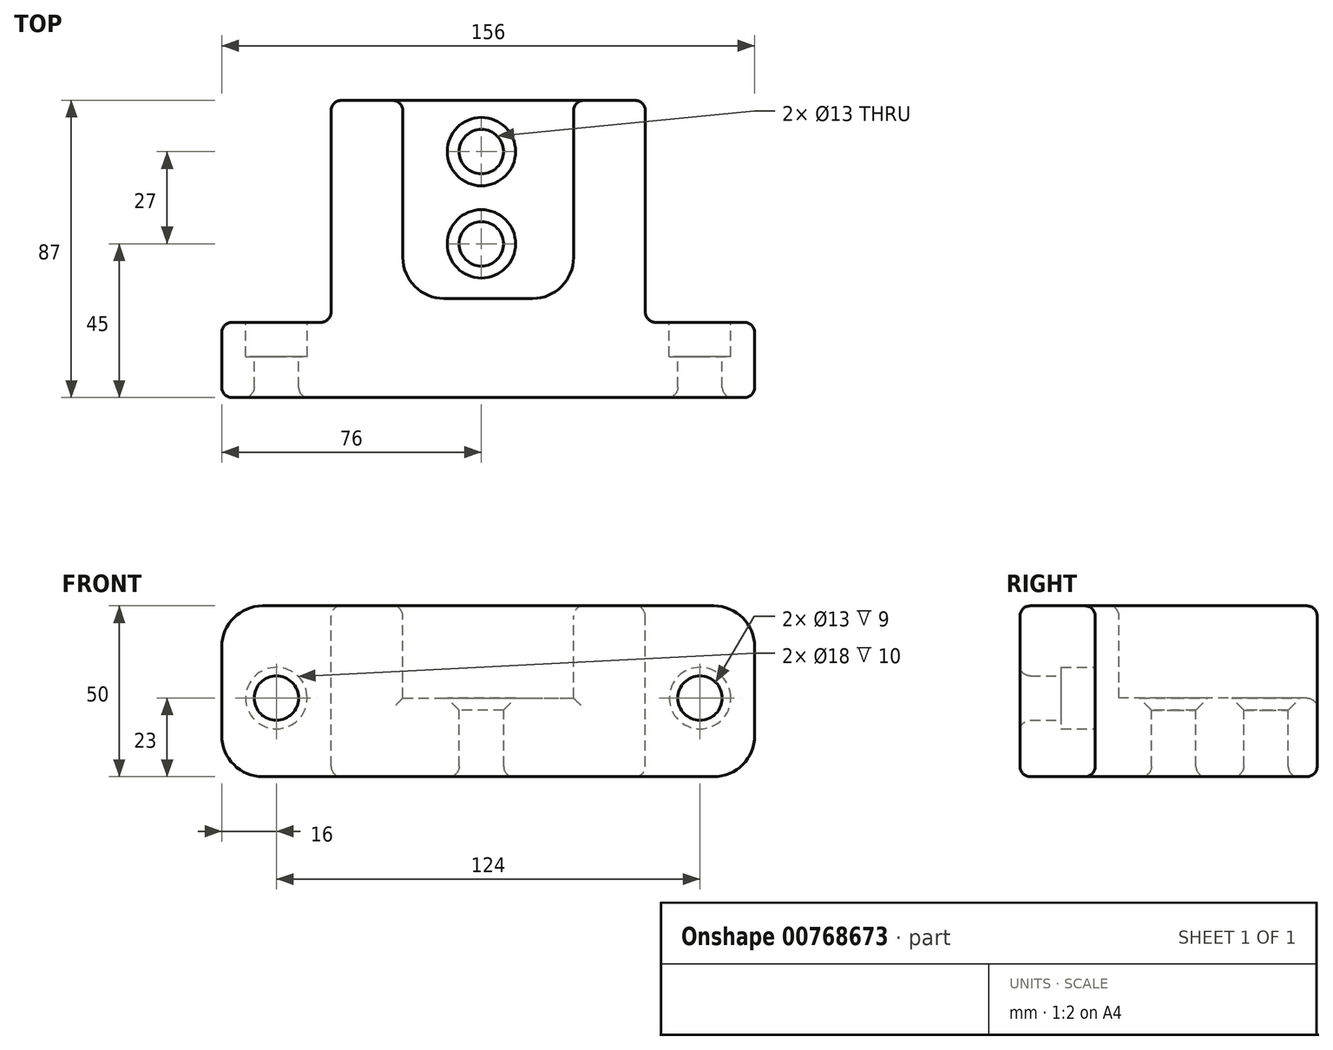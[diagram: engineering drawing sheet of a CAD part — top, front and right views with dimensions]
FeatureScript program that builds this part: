
annotation { "Feature Type Name" : "Feature", "Feature Type Description" : "" }
export const myFeature = defineFeature(function(context is Context, id is Id, definition is map)
    precondition{}
    {
        {
            var Q0;
            Q0=qCreatedBy(makeId("Front.planeOp"),FACE);
            var sketch = newSketch(context, id + "F0", { "sketchPlane" : qUnion([Q0])});
            skLineSegment(sketch, "E0.bottom", {"start": v(0, 0) * mm, "end": v(156, 0) * mm});
            skLineSegment(sketch, "E0.top", {"start": v(0, 50) * mm, "end": v(156, 50) * mm});
            skLineSegment(sketch, "E0.left", {"start": v(0, 0) * mm, "end": v(0, 50) * mm});
            skLineSegment(sketch, "E0.right", {"start": v(156, 0) * mm, "end": v(156, 50) * mm});
            skSolve(sketch);
        }
        {
            var Q0;
            Q0 = qSketchRegion(id + "F0", true);
            extrude(context, id + "F1", {"entities" : qUnion([Q0]), "depth" : 87 * mm, "offsetDistance" : 25 * mm});
        }
        {
            var Q0;
            Q0=makeQuery(id+"F1.opExtrude","SWEPT_FACE",FACE,{"disambiguationData":[OSD([sQuery(id+"F0.wireOp",EDGE,"E0.top")])]});
            var sketch = newSketch(context, id + "F2", { "sketchPlane" : qUnion([Q0])});
            skLineSegment(sketch, "E1.bottom", {"start": v(156, 0) * mm, "end": v(124, 0) * mm});
            skLineSegment(sketch, "E1.top", {"start": v(156, -65) * mm, "end": v(124, -65) * mm});
            skLineSegment(sketch, "E1.left", {"start": v(156, 0) * mm, "end": v(156, -65) * mm});
            skLineSegment(sketch, "E1.right", {"start": v(124, 0) * mm, "end": v(124, -65) * mm});
            skLineSegment(sketch, "E2.bottom", {"start": v(0, 0) * mm, "end": v(32, 0) * mm});
            skLineSegment(sketch, "E2.top", {"start": v(0, -65) * mm, "end": v(32, -65) * mm});
            skLineSegment(sketch, "E2.left", {"start": v(0, 0) * mm, "end": v(0, -65) * mm});
            skLineSegment(sketch, "E2.right", {"start": v(32, 0) * mm, "end": v(32, -65) * mm});
            skSolve(sketch);
        }
        {
            var Q0;
            Q0 = qSketchRegion(id + "F2", true);
            extrude(context, id + "F3", {"entities" : qUnion([Q0]), "operationType" : NewBodyOperationType.REMOVE, "endBound" : BoundingType.UP_TO_NEXT, "oppositeDirection" : true, "depth" : 25 * mm, "offsetDistance" : 25 * mm});
        }
        {
            var Q0;
            Q0=makeQuery(id+"F1.opExtrude","SWEPT_FACE",FACE,{"disambiguationData":[OSD([sQuery(id+"F0.wireOp",EDGE,"E0.top")])]});
            var sketch = newSketch(context, id + "F4", { "sketchPlane" : qUnion([Q0])});
            skLineSegment(sketch, "E3.bottom", {"start": v(53, 0) * mm, "end": v(103, 0) * mm});
            skLineSegment(sketch, "E3.top", {"start": v(53, -58) * mm, "end": v(103, -58) * mm});
            skLineSegment(sketch, "E3.left", {"start": v(53, 0) * mm, "end": v(53, -58) * mm});
            skLineSegment(sketch, "E3.right", {"start": v(103, 0) * mm, "end": v(103, -58) * mm});
            skSolve(sketch);
        }
        {
            var Q0;
            Q0 = qSketchRegion(id + "F4", true);
            extrude(context, id + "F5", {"entities" : qUnion([Q0]), "operationType" : NewBodyOperationType.REMOVE, "oppositeDirection" : true, "depth" : 27 * mm, "offsetDistance" : 25 * mm});
        }
        {
            var Q0;
            Q0=makeQuery(id+"F3.boolean.opBoolean","COPY",FACE,{"derivedFrom":makeQuery(id+"F3.opExtrude","SWEPT_FACE",FACE,{"disambiguationData":[OSD([sQuery(id+"F2.wireOp",EDGE,"E1.top")])]})});
            var sketch = newSketch(context, id + "F6", { "sketchPlane" : qUnion([Q0])});
            skPoint(sketch, "E4", {"position": v(-140, 23) * mm});
            skPoint(sketch, "E5", {"position": v(-16, 23) * mm});
            skSolve(sketch);
        }
        {
            var Q0;
            Q0=sQuery(id+"F6.wireOp",VERTEX,"E4");
            var Q1;
            Q1=sQuery(id+"F6.wireOp",VERTEX,"E5");
            var Q2;
            Q2=makeQuery(id+"F1.opExtrude","SWEPT_BODY",BODY,{"disambiguationData":[OSD([sQuery(id+"F0.wireOp",EDGE,"E0.bottom"),sQuery(id+"F0.wireOp",EDGE,"E0.top"),sQuery(id+"F0.wireOp",EDGE,"E0.left"),sQuery(id+"F0.wireOp",EDGE,"E0.right")])]});
            hole(context, id + "F7", {"style" : HoleStyle.C_BORE, "endStyle" : HoleEndStyle.THROUGH, "holeDiameter" : 13 * mm, "cBoreDiameter" : 18 * mm, "cBoreDepth" : 10 * mm, "majorDiameter" : 5 * mm, "isTappedThrough" : true, "tappedDepth" : 12 * mm, "tapClearance" : 3, "locations" : qUnion([Q0, Q1]), "scope" : qUnion([Q2])});
        }
        {
            var Q0;
            Q0=makeQuery(id+"F5.boolean.opBoolean","COPY",FACE,{"derivedFrom":makeQuery(id+"F5.opExtrude","CAP_FACE",FACE,{"disambiguationData":[OSD([sQuery(id+"F4.wireOp",EDGE,"E3.bottom"),sQuery(id+"F4.wireOp",EDGE,"E3.top"),sQuery(id+"F4.wireOp",EDGE,"E3.left"),sQuery(id+"F4.wireOp",EDGE,"E3.right")])],"isStart":false})});
            var sketch = newSketch(context, id + "F8", { "sketchPlane" : qUnion([Q0])});
            skPoint(sketch, "E6", {"position": v(76, -15) * mm});
            skPoint(sketch, "E7", {"position": v(76, -42) * mm});
            skSolve(sketch);
        }
        {
            var Q0;
            Q0=sQuery(id+"F8.wireOp",VERTEX,"E6");
            var Q1;
            Q1=sQuery(id+"F8.wireOp",VERTEX,"E7");
            var Q2;
            Q2=makeQuery(id+"F1.opExtrude","SWEPT_BODY",BODY,{"disambiguationData":[OSD([sQuery(id+"F0.wireOp",EDGE,"E0.bottom"),sQuery(id+"F0.wireOp",EDGE,"E0.top"),sQuery(id+"F0.wireOp",EDGE,"E0.left"),sQuery(id+"F0.wireOp",EDGE,"E0.right")])]});
            hole(context, id + "F9", {"style" : HoleStyle.C_SINK, "endStyle" : HoleEndStyle.THROUGH, "holeDiameter" : 13 * mm, "cSinkDiameter" : 20 * mm, "cSinkAngle" : 90 * degree, "majorDiameter" : 5 * mm, "isTappedThrough" : true, "tappedDepth" : 12 * mm, "tapClearance" : 3, "locations" : qUnion([Q0, Q1]), "scope" : qUnion([Q2])});
        }
        {
            var Q0;
            Q0=makeQuery(id+"F1.opExtrude","SWEPT_EDGE",EDGE,{"disambiguationData":[OSD([sQuery(id+"F0.wireOp",EDGE,"E0.top"),sQuery(id+"F0.wireOp",EDGE,"E0.right")])]});
            var Q1;
            Q1=makeQuery(id+"F1.opExtrude","SWEPT_EDGE",EDGE,{"disambiguationData":[OSD([sQuery(id+"F0.wireOp",EDGE,"E0.bottom"),sQuery(id+"F0.wireOp",EDGE,"E0.right")])]});
            var Q2;
            Q2=makeQuery(id+"F1.opExtrude","SWEPT_EDGE",EDGE,{"disambiguationData":[OSD([sQuery(id+"F0.wireOp",EDGE,"E0.top"),sQuery(id+"F0.wireOp",EDGE,"E0.left")])]});
            var Q3;
            Q3=makeQuery(id+"F1.opExtrude","SWEPT_EDGE",EDGE,{"disambiguationData":[OSD([sQuery(id+"F0.wireOp",EDGE,"E0.bottom"),sQuery(id+"F0.wireOp",EDGE,"E0.left")])]});
            var Q4;
            Q4=makeQuery(id+"F5.boolean.opBoolean","COPY",EDGE,{"derivedFrom":makeQuery(id+"F5.opExtrude","SWEPT_EDGE",EDGE,{"disambiguationData":[OSD([sQuery(id+"F4.wireOp",EDGE,"E3.top"),sQuery(id+"F4.wireOp",EDGE,"E3.left")])]})});
            var Q5;
            Q5=makeQuery(id+"F5.boolean.opBoolean","COPY",EDGE,{"derivedFrom":makeQuery(id+"F5.opExtrude","SWEPT_EDGE",EDGE,{"disambiguationData":[OSD([sQuery(id+"F4.wireOp",EDGE,"E3.top"),sQuery(id+"F4.wireOp",EDGE,"E3.right")])]})});
            fillet(context, id + "F10", {"entities" : qUnion([Q0, Q1, Q2, Q3, Q4, Q5]), "radius" : 12 * mm, "tangentPropagation" : true, "allowEdgeOverflow" : false});
        }
        {
            var Q0;
            Q0=makeQuery(id+"F1.opExtrude","CAP_FACE",FACE,{"disambiguationData":[OSD([sQuery(id+"F0.wireOp",EDGE,"E0.bottom"),sQuery(id+"F0.wireOp",EDGE,"E0.top"),sQuery(id+"F0.wireOp",EDGE,"E0.left"),sQuery(id+"F0.wireOp",EDGE,"E0.right")])],"isStart":true});
            var Q1;
            Q1=makeQuery(id+"F1.opExtrude","SWEPT_FACE",FACE,{"disambiguationData":[OSD([sQuery(id+"F0.wireOp",EDGE,"E0.top")])]});
            var Q2;
            Q2=makeQuery(id+"F3.boolean.opBoolean","COPY",FACE,{"derivedFrom":makeQuery(id+"F3.opExtrude","SWEPT_FACE",FACE,{"disambiguationData":[OSD([sQuery(id+"F2.wireOp",EDGE,"E2.right")])]})});
            var Q3;
            Q3=makeQuery(id+"F3.boolean.opBoolean","COPY",FACE,{"derivedFrom":makeQuery(id+"F3.opExtrude","SWEPT_FACE",FACE,{"disambiguationData":[OSD([sQuery(id+"F2.wireOp",EDGE,"E1.right")])]})});
            var Q4;
            Q4=makeQuery(id+"F1.opExtrude","SWEPT_FACE",FACE,{"disambiguationData":[OSD([sQuery(id+"F0.wireOp",EDGE,"E0.bottom")])]});
            var Q5;
            Q5=makeQuery(id+"F1.opExtrude","CAP_FACE",FACE,{"disambiguationData":[OSD([sQuery(id+"F0.wireOp",EDGE,"E0.bottom"),sQuery(id+"F0.wireOp",EDGE,"E0.top"),sQuery(id+"F0.wireOp",EDGE,"E0.left"),sQuery(id+"F0.wireOp",EDGE,"E0.right")])],"isStart":false});
            fillet(context, id + "F11", {"entities" : qUnion([Q0, Q1, Q2, Q3, Q4, Q5]), "radius" : 3 * mm, "tangentPropagation" : true, "allowEdgeOverflow" : false});
        }
    });
